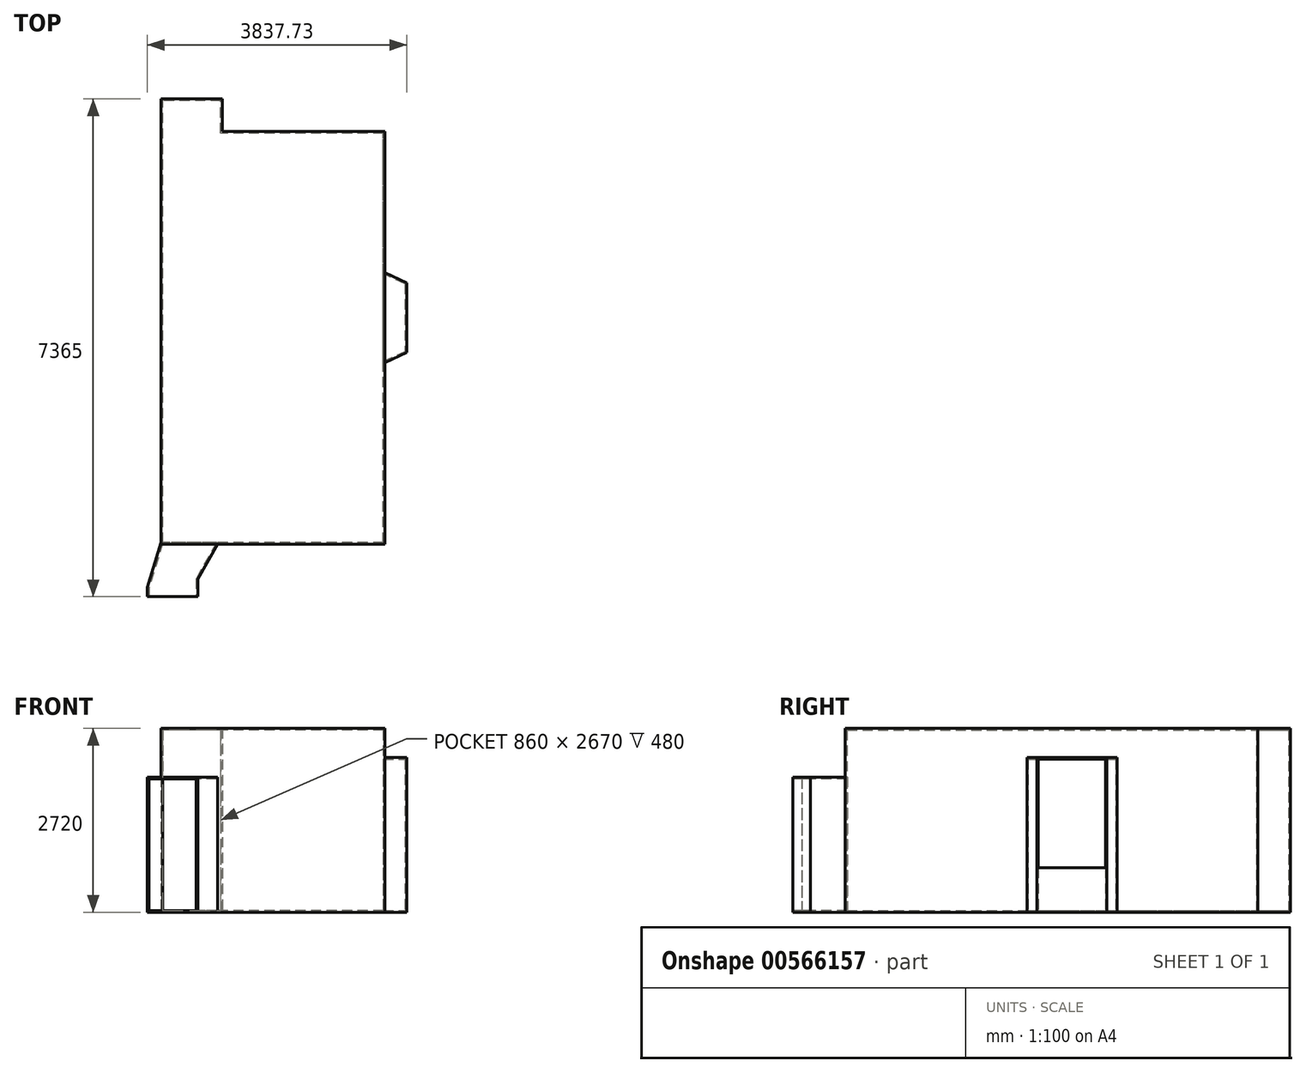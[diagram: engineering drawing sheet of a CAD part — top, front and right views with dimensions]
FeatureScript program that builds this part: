
annotation { "Feature Type Name" : "Feature", "Feature Type Description" : "" }
export const myFeature = defineFeature(function(context is Context, id is Id, definition is map)
    precondition{}
    {
        {
            var Q0;
            Q0=qCreatedBy(makeId("Top.planeOp"),FACE);
            var sketch = newSketch(context, id + "F0", { "sketchPlane" : qUnion([Q0])});
            skLineSegment(sketch, "E0.bottom", {"start": v(0, 0) * mm, "end": v(-2465, 0) * mm});
            skLineSegment(sketch, "E0.top", {"start": v(0, 6060) * mm, "end": v(-2405, 6060) * mm});
            skLineSegment(sketch, "E0.left", {"start": v(0, 0) * mm, "end": v(0, 2680) * mm});
            skLineSegment(sketch, "E1", {"start": v(0, 2680) * mm, "end": v(320, 2830) * mm});
            skLineSegment(sketch, "E2", {"start": v(320, 2830) * mm, "end": v(320, 3830) * mm});
            skLineSegment(sketch, "E3", {"start": v(320, 3830) * mm, "end": v(0, 3980) * mm});
            skLineSegment(sketch, "E4.trimOffspring", {"start": v(0, 3980) * mm, "end": v(0, 6060) * mm});
            skLineSegment(sketch, "E5", {"start": v(-3265, 0) * mm, "end": v(-3467.73, -670) * mm});
            skLineSegment(sketch, "E6", {"start": v(-3467.73, -670) * mm, "end": v(-3467.73, -800) * mm});
            skLineSegment(sketch, "E7", {"start": v(-2465, 0) * mm, "end": v(-2767.73, -535) * mm});
            skLineSegment(sketch, "E8", {"start": v(-2767.73, -535) * mm, "end": v(-2767.73, -800) * mm});
            skLineSegment(sketch, "E9", {"start": v(-2767.73, -800) * mm, "end": v(-3467.73, -800) * mm});
            skLineSegment(sketch, "E10", {"start": v(-2405, 6060) * mm, "end": v(-2405, 6540) * mm});
            skLineSegment(sketch, "E11", {"start": v(-2405, 6540) * mm, "end": v(-3265, 6540) * mm});
            skLineSegment(sketch, "E12", {"start": v(-3265, 0) * mm, "end": v(-3265, 6540) * mm});
            skSolve(sketch);
        }
        {
            var Q0;
            Q0 = qSketchRegion(id + "F0", true);
            extrude(context, id + "F1", {"entities" : qUnion([Q0]), "depth" : 2670 * mm, "offsetDistance" : 25 * mm});
        }
        {
            var Q0;
            Q0=makeQuery(id+"F1.opExtrude","CAP_FACE",FACE,{"disambiguationData":[OSD([sQuery(id+"F0.wireOp",EDGE,"E0.bottom"),sQuery(id+"F0.wireOp",EDGE,"E0.top"),sQuery(id+"F0.wireOp",EDGE,"E0.left"),sQuery(id+"F0.wireOp",EDGE,"E1"),sQuery(id+"F0.wireOp",EDGE,"E2"),sQuery(id+"F0.wireOp",EDGE,"E3"),sQuery(id+"F0.wireOp",EDGE,"E4.trimOffspring"),sQuery(id+"F0.wireOp",EDGE,"E5"),sQuery(id+"F0.wireOp",EDGE,"E6"),sQuery(id+"F0.wireOp",EDGE,"E7"),sQuery(id+"F0.wireOp",EDGE,"E8"),sQuery(id+"F0.wireOp",EDGE,"E9"),sQuery(id+"F0.wireOp",EDGE,"E10"),sQuery(id+"F0.wireOp",EDGE,"E11"),sQuery(id+"F0.wireOp",EDGE,"E12")])],"isStart":true});
            cPlane(context, id + "F2", {"entities" : qUnion([Q0]), "cplaneType" : CPlaneType.OFFSET, "offset" : 1950 * mm, "oppositeDirection" : true, "width" : 150 * mm, "height" : 150 * mm});
        }
        {
            var Q0;
            Q0=qCreatedBy(id+"F2.planeOp",FACE);
            var sketch = newSketch(context, id + "F3", { "sketchPlane" : qUnion([Q0])});
            skLineSegment(sketch, "E13.0", {"start": v(-3265, 0) * mm, "end": v(-3467.73, 670) * mm});
            skLineSegment(sketch, "E14.0", {"start": v(-2767.73, 800) * mm, "end": v(-3467.73, 800) * mm});
            skLineSegment(sketch, "E15.0", {"start": v(-2767.73, 535) * mm, "end": v(-2767.73, 800) * mm});
            skLineSegment(sketch, "E16.0", {"start": v(-2465, 0) * mm, "end": v(-2767.73, 535) * mm});
            skLineSegment(sketch, "E17", {"start": v(-2465, 0) * mm, "end": v(-3265, 0) * mm});
            skLineSegment(sketch, "E18.0", {"start": v(-3467.73, 670) * mm, "end": v(-3467.73, 800) * mm});
            skSolve(sketch);
        }
        {
            var Q0;
            Q0 = qSketchRegion(id + "F3", true);
            extrude(context, id + "F4", {"entities" : qUnion([Q0]), "operationType" : NewBodyOperationType.REMOVE, "endBound" : BoundingType.UP_TO_NEXT, "oppositeDirection" : true, "depth" : 25 * mm, "offsetDistance" : 25 * mm});
        }
        {
            var Q0;
            Q0=makeQuery(id+"F1.opExtrude","CAP_FACE",FACE,{"disambiguationData":[OSD([sQuery(id+"F0.wireOp",EDGE,"E0.bottom"),sQuery(id+"F0.wireOp",EDGE,"E0.top"),sQuery(id+"F0.wireOp",EDGE,"E0.left"),sQuery(id+"F0.wireOp",EDGE,"E1"),sQuery(id+"F0.wireOp",EDGE,"E2"),sQuery(id+"F0.wireOp",EDGE,"E3"),sQuery(id+"F0.wireOp",EDGE,"E4.trimOffspring"),sQuery(id+"F0.wireOp",EDGE,"E5"),sQuery(id+"F0.wireOp",EDGE,"E6"),sQuery(id+"F0.wireOp",EDGE,"E7"),sQuery(id+"F0.wireOp",EDGE,"E8"),sQuery(id+"F0.wireOp",EDGE,"E9"),sQuery(id+"F0.wireOp",EDGE,"E10"),sQuery(id+"F0.wireOp",EDGE,"E11"),sQuery(id+"F0.wireOp",EDGE,"E12")])],"isStart":true});
            cPlane(context, id + "F5", {"entities" : qUnion([Q0]), "cplaneType" : CPlaneType.OFFSET, "offset" : 2240 * mm, "oppositeDirection" : true, "width" : 150 * mm, "height" : 150 * mm});
        }
        {
            var Q0;
            Q0=qCreatedBy(id+"F5.planeOp",FACE);
            var sketch = newSketch(context, id + "F6", { "sketchPlane" : qUnion([Q0])});
            skLineSegment(sketch, "E19.0", {"start": v(320, -2830) * mm, "end": v(320, -3830) * mm});
            skLineSegment(sketch, "E20.0", {"start": v(0, -2680) * mm, "end": v(320, -2830) * mm});
            skLineSegment(sketch, "E21.0", {"start": v(320, -3830) * mm, "end": v(0, -3980) * mm});
            skLineSegment(sketch, "E22", {"start": v(0, -2680) * mm, "end": v(0, -3980) * mm});
            skSolve(sketch);
        }
        {
            var Q0;
            Q0 = qSketchRegion(id + "F6", true);
            extrude(context, id + "F7", {"entities" : qUnion([Q0]), "operationType" : NewBodyOperationType.REMOVE, "endBound" : BoundingType.UP_TO_NEXT, "oppositeDirection" : true, "depth" : 25 * mm, "offsetDistance" : 25 * mm});
        }
        {
            var Q0;
            Q0=makeQuery(id+"F1.opExtrude","SWEPT_FACE",FACE,{"disambiguationData":[OSD([sQuery(id+"F0.wireOp",EDGE,"E9")])]});
            shell(context, id + "F8", {"entities" : qUnion([Q0]), "thickness" : 25 * mm, "oppositeDirection" : true});
        }
        {
            var Q0;
            Q0=makeQuery(id+"F8.opShell","OFFSET_FACE",FACE,{"disambiguationData":[OSD([sQuery(id+"F0.wireOp",EDGE,"E2")])]});
            var sketch = newSketch(context, id + "F9", { "sketchPlane" : qUnion([Q0])});
            skLineSegment(sketch, "E23.bottom", {"start": v(-3830, 2240) * mm, "end": v(-2830, 2240) * mm});
            skLineSegment(sketch, "E23.top", {"start": v(-3830, 630) * mm, "end": v(-2830, 630) * mm});
            skLineSegment(sketch, "E23.left", {"start": v(-3830, 2240) * mm, "end": v(-3830, 630) * mm});
            skLineSegment(sketch, "E23.right", {"start": v(-2830, 2240) * mm, "end": v(-2830, 630) * mm});
            skSolve(sketch);
        }
        {
            var Q0;
            Q0 = qSketchRegion(id + "F9", true);
            extrude(context, id + "F10", {"entities" : qUnion([Q0]), "operationType" : NewBodyOperationType.REMOVE, "endBound" : BoundingType.UP_TO_NEXT, "oppositeDirection" : true, "depth" : 25 * mm, "offsetDistance" : 25 * mm});
        }
    });
